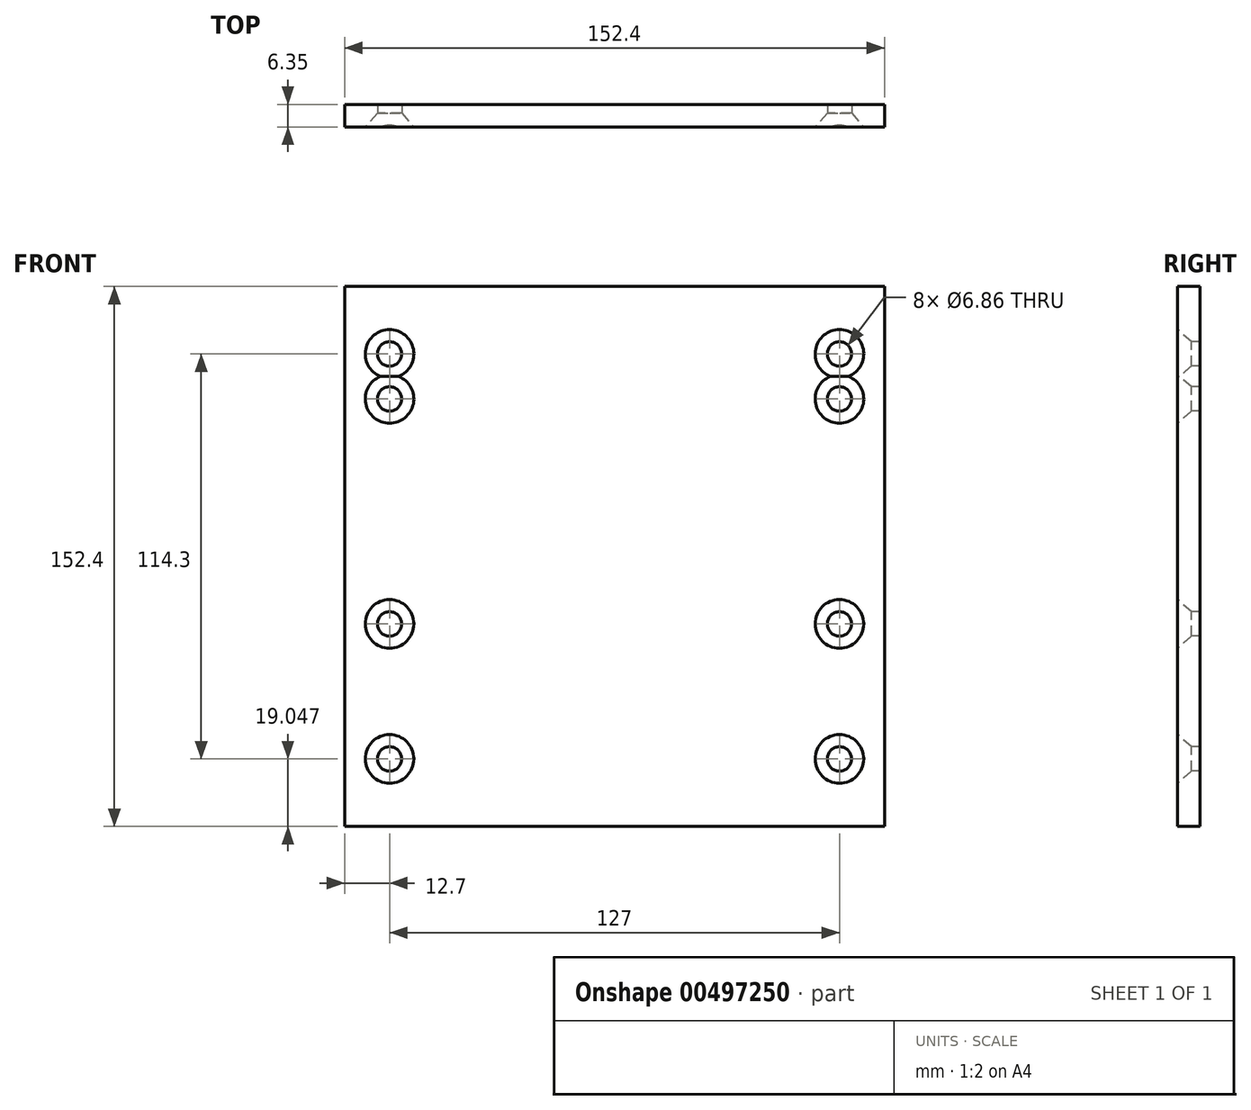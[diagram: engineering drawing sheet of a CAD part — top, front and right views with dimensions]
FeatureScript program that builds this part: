
annotation { "Feature Type Name" : "Feature", "Feature Type Description" : "" }
export const myFeature = defineFeature(function(context is Context, id is Id, definition is map)
    precondition{}
    {
        {
            var Q0;
            Q0=qCreatedBy(makeId("Front.planeOp"),FACE);
            var sketch = newSketch(context, id + "F0", { "sketchPlane" : qUnion([Q0])});
            skLineSegment(sketch, "E0.bottom", {"start": v(-69.84, 71.15) * mm, "end": v(82.56, 71.15) * mm});
            skLineSegment(sketch, "E0.top", {"start": v(-69.84, -81.25) * mm, "end": v(82.56, -81.25) * mm});
            skLineSegment(sketch, "E0.left", {"start": v(-69.84, 71.15) * mm, "end": v(-69.84, -81.25) * mm});
            skLineSegment(sketch, "E0.right", {"start": v(82.56, 71.15) * mm, "end": v(82.56, -81.25) * mm});
            skSolve(sketch);
        }
        {
            var Q0;
            Q0 = qSketchRegion(id + "F0", true);
            extrude(context, id + "F1", {"entities" : qUnion([Q0]), "depth" : 6.35 * mm});
        }
        {
            var Q0;
            Q0=makeQuery(id+"F1.opExtrude","CAP_FACE",FACE,{"disambiguationData":[OSD([sQuery(id+"F0.wireOp",EDGE,"E0.bottom"),sQuery(id+"F0.wireOp",EDGE,"E0.top"),sQuery(id+"F0.wireOp",EDGE,"E0.left"),sQuery(id+"F0.wireOp",EDGE,"E0.right")])],"isStart":false});
            var sketch = newSketch(context, id + "F2", { "sketchPlane" : qUnion([Q0])});
            skPoint(sketch, "E1", {"position": v(-57.14, 52.1) * mm});
            skPoint(sketch, "E2", {"position": v(-57.14, -24.1) * mm});
            skPoint(sketch, "E3", {"position": v(-57.14, -62.2) * mm});
            skPoint(sketch, "E4", {"position": v(-57.14, 39.4) * mm});
            skPoint(sketch, "E5", {"position": v(69.86, 52.1) * mm});
            skPoint(sketch, "E6", {"position": v(69.86, 39.4) * mm});
            skPoint(sketch, "E7", {"position": v(69.86, -24.1) * mm});
            skPoint(sketch, "E8", {"position": v(69.86, -62.2) * mm});
            skSolve(sketch);
        }
        {
            var Q0;
            Q0=sQuery(id+"F2.wireOp",VERTEX,"E1");
            var Q1;
            Q1=sQuery(id+"F2.wireOp",VERTEX,"E4");
            var Q2;
            Q2=sQuery(id+"F2.wireOp",VERTEX,"E5");
            var Q3;
            Q3=sQuery(id+"F2.wireOp",VERTEX,"E6");
            var Q4;
            Q4=sQuery(id+"F2.wireOp",VERTEX,"E7");
            var Q5;
            Q5=sQuery(id+"F2.wireOp",VERTEX,"E8");
            var Q6;
            Q6=sQuery(id+"F2.wireOp",VERTEX,"E3");
            var Q7;
            Q7=sQuery(id+"F2.wireOp",VERTEX,"E2");
            var Q8;
            Q8=makeQuery(id+"F1.opExtrude","SWEPT_BODY",BODY,{"disambiguationData":[OSD([sQuery(id+"F0.wireOp",EDGE,"E0.bottom"),sQuery(id+"F0.wireOp",EDGE,"E0.top"),sQuery(id+"F0.wireOp",EDGE,"E0.left"),sQuery(id+"F0.wireOp",EDGE,"E0.right")])]});
            hole(context, id + "F3", {"style" : HoleStyle.C_SINK, "endStyle" : HoleEndStyle.THROUGH, "holeDiameter" : 6.86 * mm, "cSinkDiameter" : 13.72 * mm, "cSinkAngle" : 82 * degree, "isTappedThrough" : true, "tappedDepth" : 12.7 * mm, "tapClearance" : 3, "startFromSketch" : true, "locations" : qUnion([Q0, Q1, Q2, Q3, Q4, Q5, Q6, Q7]), "scope" : qUnion([Q8])});
        }
    });
